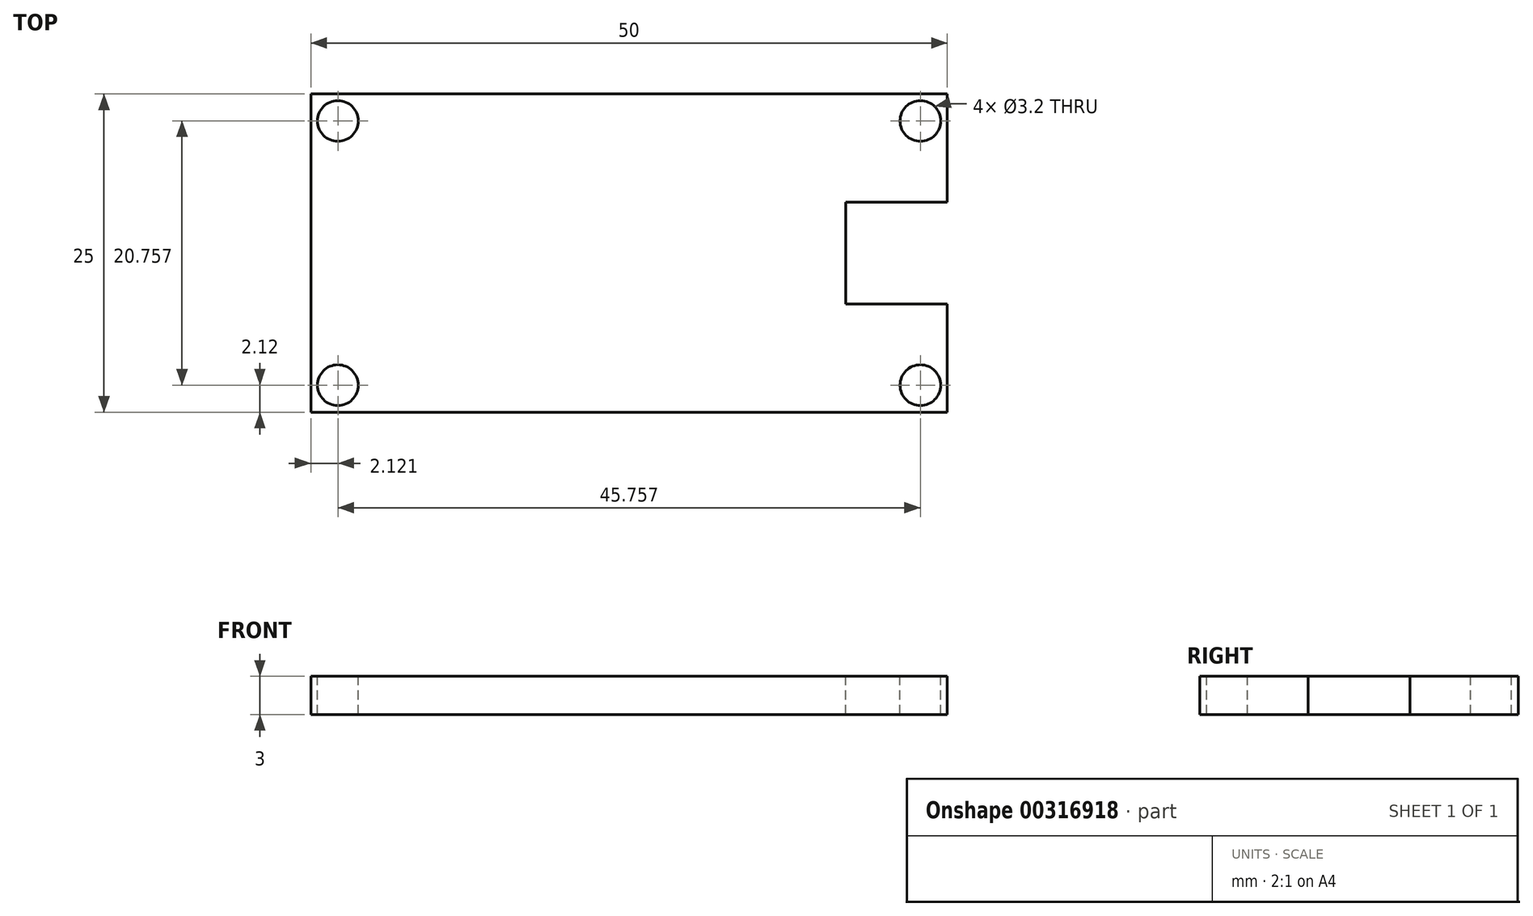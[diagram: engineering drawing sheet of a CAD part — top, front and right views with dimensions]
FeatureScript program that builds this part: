
annotation { "Feature Type Name" : "Feature", "Feature Type Description" : "" }
export const myFeature = defineFeature(function(context is Context, id is Id, definition is map)
    precondition{}
    {
        {
            var Q0;
            Q0=qCreatedBy(makeId("Top.planeOp"),FACE);
            var sketch = newSketch(context, id + "F0", { "sketchPlane" : qUnion([Q0])});
            skLineSegment(sketch, "E0.bottom", {"start": v(0, -1.45) * mm, "end": v(50, -1.45) * mm});
            skLineSegment(sketch, "E0.top", {"start": v(0, 23.55) * mm, "end": v(50, 23.55) * mm});
            skLineSegment(sketch, "E0.left", {"start": v(0, -1.45) * mm, "end": v(0, 23.55) * mm});
            skLineSegment(sketch, "E0.right", {"start": v(50, -1.45) * mm, "end": v(50, 23.55) * mm});
            skSolve(sketch);
        }
        {
            var Q0;
            Q0=makeQuery(id+"F0.imprint","IMPRINT",FACE,{"disambiguationData":[TD([[makeQuery(id+"F0.imprint","IMPRINT",EDGE,{"derivedFrom":sQuery(id+"F0.wireOp",EDGE,"E0.bottom")}),1.0]])]});
            extrude(context, id + "F1", {"entities" : qUnion([Q0]), "depth" : 3 * mm});
        }
        {
            var Q0;
            Q0=makeQuery(id+"F1.opExtrude","CAP_FACE",FACE,{"disambiguationData":[OSD([sQuery(id+"F0.wireOp",EDGE,"E0.bottom"),sQuery(id+"F0.wireOp",EDGE,"E0.top"),sQuery(id+"F0.wireOp",EDGE,"E0.left"),sQuery(id+"F0.wireOp",EDGE,"E0.right")])],"isStart":false});
            var sketch = newSketch(context, id + "F2", { "sketchPlane" : qUnion([Q0])});
            skLineSegment(sketch, "E1", {"start": v(0, 23.55) * mm, "end": v(2.12, 21.43) * mm});
            skLineSegment(sketch, "E2", {"start": v(50, 23.55) * mm, "end": v(47.88, 21.43) * mm});
            skLineSegment(sketch, "E3", {"start": v(50, -1.45) * mm, "end": v(47.88, 0.67) * mm});
            skLineSegment(sketch, "E4", {"start": v(0, -1.45) * mm, "end": v(2.12, 0.67) * mm});
            skSolve(sketch);
        }
        {
            var Q0;
            Q0=sQuery(id+"F2.wireOp",VERTEX,"E1.end");
            var Q1;
            Q1=sQuery(id+"F2.wireOp",VERTEX,"E2.end");
            var Q2;
            Q2=sQuery(id+"F2.wireOp",VERTEX,"E3.end");
            var Q3;
            Q3=sQuery(id+"F2.wireOp",VERTEX,"E4.end");
            var Q4;
            Q4=makeQuery(id+"F1.opExtrude","SWEPT_BODY",BODY,{"disambiguationData":[OSD([sQuery(id+"F0.wireOp",EDGE,"E0.bottom"),sQuery(id+"F0.wireOp",EDGE,"E0.top"),sQuery(id+"F0.wireOp",EDGE,"E0.left"),sQuery(id+"F0.wireOp",EDGE,"E0.right")])]});
            hole(context, id + "F3", {"style" : HoleStyle.SIMPLE, "endStyle" : HoleEndStyle.THROUGH, "holeDiameter" : 3.2 * mm, "isTappedThrough" : true, "tappedDepth" : 12 * mm, "tapClearance" : 3, "locations" : qUnion([Q0, Q1, Q2, Q3]), "scope" : qUnion([Q4])});
        }
        {
            var Q0;
            Q0=makeQuery(id+"F1.opExtrude","CAP_FACE",FACE,{"disambiguationData":[OSD([sQuery(id+"F0.wireOp",EDGE,"E0.bottom"),sQuery(id+"F0.wireOp",EDGE,"E0.top"),sQuery(id+"F0.wireOp",EDGE,"E0.left"),sQuery(id+"F0.wireOp",EDGE,"E0.right")])],"isStart":false});
            var sketch = newSketch(context, id + "F4", { "sketchPlane" : qUnion([Q0])});
            skPoint(sketch, "E5", {"position": v(50, 11.05) * mm});
            skLineSegment(sketch, "E6", {"start": v(50, 11.05) * mm, "end": v(50, 15.05) * mm});
            skLineSegment(sketch, "E7", {"start": v(50, 11.05) * mm, "end": v(50, 7.05) * mm});
            skLineSegment(sketch, "E8", {"start": v(50, 15.05) * mm, "end": v(42, 15.05) * mm});
            skLineSegment(sketch, "E9", {"start": v(50, 7.05) * mm, "end": v(42, 7.05) * mm});
            skLineSegment(sketch, "E10", {"start": v(42, 7.05) * mm, "end": v(42, 15.05) * mm});
            skSolve(sketch);
        }
        {
            var Q0;
            Q0=makeQuery(id+"F4.imprint","IMPRINT",FACE,{"disambiguationData":[TD([[makeQuery(id+"F4.imprint","IMPRINT",EDGE,{"derivedFrom":sQuery(id+"F4.wireOp",EDGE,"E6")}),1.0]])]});
            extrude(context, id + "F5", {"entities" : qUnion([Q0]), "operationType" : NewBodyOperationType.REMOVE, "oppositeDirection" : true, "depth" : 25 * mm});
        }
    });
